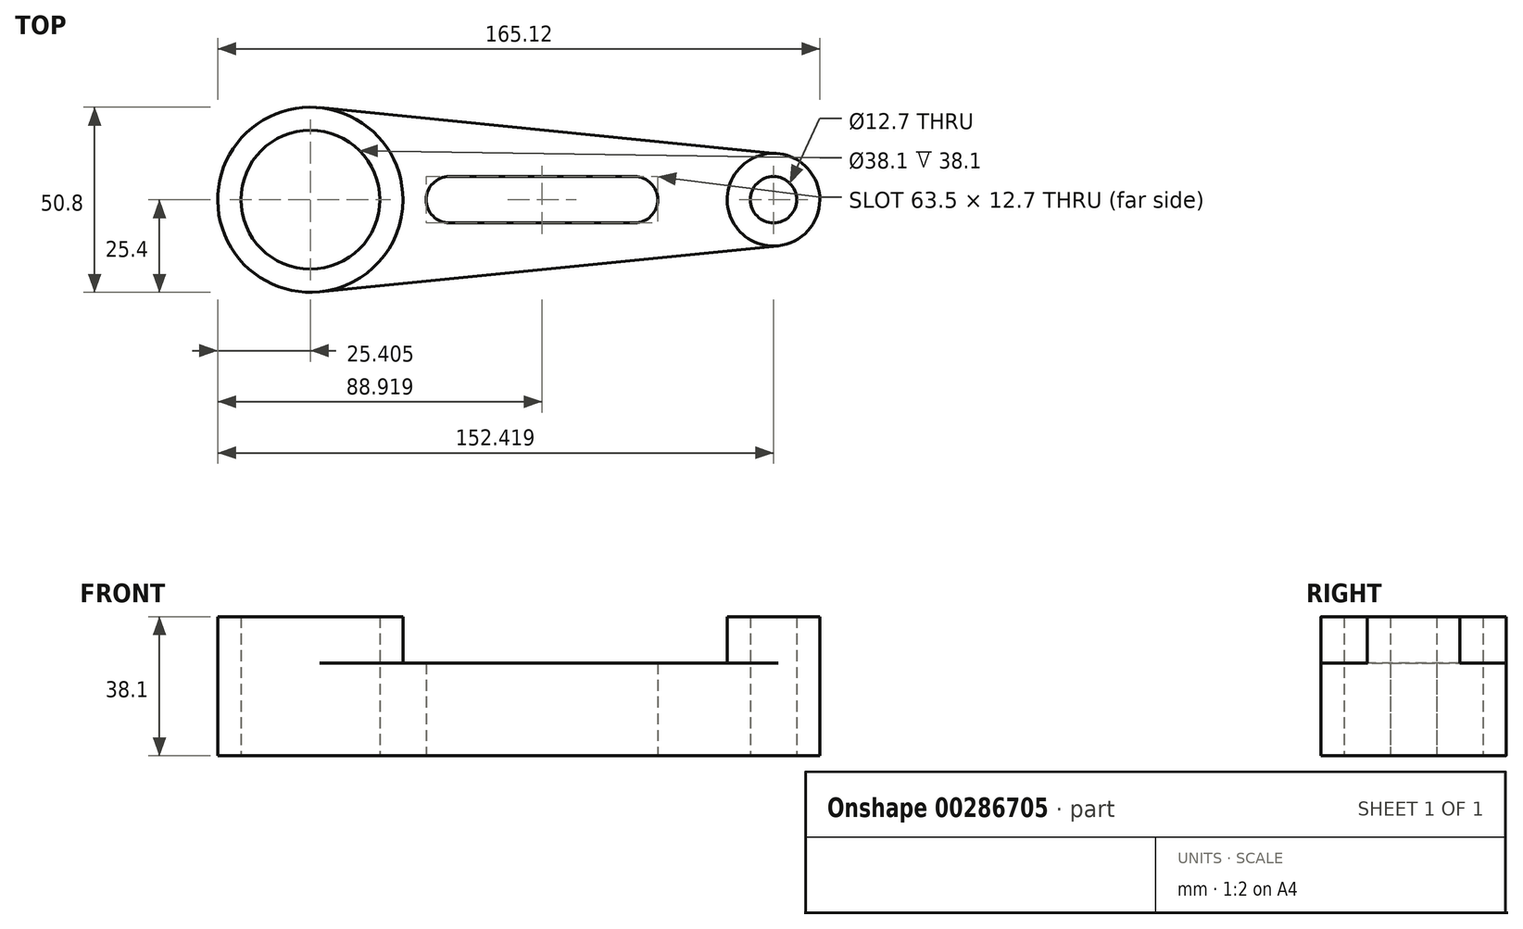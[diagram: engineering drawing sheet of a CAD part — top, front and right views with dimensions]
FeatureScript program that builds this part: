
annotation { "Feature Type Name" : "Feature", "Feature Type Description" : "" }
export const myFeature = defineFeature(function(context is Context, id is Id, definition is map)
    precondition{}
    {
        {
            var Q0;
            Q0=qCreatedBy(makeId("Top.planeOp"),FACE);
            var sketch = newSketch(context, id + "F0", { "sketchPlane" : qUnion([Q0])});
            skCircle(sketch, "E0", {"center": v(108.8, 0) * mm, "radius": 6.35 * mm});
            skCircle(sketch, "E1", {"center": v(108.8, 0) * mm, "radius": 12.7 * mm});
            skCircle(sketch, "E2", {"center": v(-18.2, 0) * mm, "radius": 19.05 * mm});
            skCircle(sketch, "E3", {"center": v(-18.2, 0) * mm, "radius": 25.4 * mm});
            skLineSegment(sketch, "E4", {"start": v(-15.67, 25.27) * mm, "end": v(110.08, 12.64) * mm});
            skLineSegment(sketch, "E5", {"start": v(-15.67, -25.27) * mm, "end": v(110.08, -12.64) * mm});
            skCircle(sketch, "E6", {"center": v(70.7, 0) * mm, "radius": 6.35 * mm});
            skCircle(sketch, "E7", {"center": v(19.9, 0) * mm, "radius": 6.35 * mm});
            skLineSegment(sketch, "E8", {"start": v(19.9, -6.35) * mm, "end": v(70.7, -6.35) * mm});
            skLineSegment(sketch, "E9", {"start": v(19.9, 6.35) * mm, "end": v(70.7, 6.35) * mm});
            skSolve(sketch);
        }
        {
            var Q0;
            {var subQ1=sQuery(id+"F0.wireOp",EDGE,"E4");Q0=makeQuery(id+"F0.imprint","IMPRINT",FACE,{"disambiguationData":[TD([[makeQuery(id+"F0.imprint","IMPRINT",EDGE,{"derivedFrom":subQ1}),-1.0]])]});}
            extrude(context, id + "F1", {"entities" : qUnion([Q0]), "depth" : 25.4 * mm});
        }
        {
            var Q0;
            Q0=makeQuery(id+"F0.imprint","IMPRINT",FACE,{"disambiguationData":[TD([[makeQuery(id+"F0.imprint","IMPRINT",EDGE,{"derivedFrom":sQuery(id+"F0.wireOp",EDGE,"E2")}),-1.0]])]});
            var Q1;
            Q1=makeQuery(id+"F0.imprint","IMPRINT",FACE,{"disambiguationData":[TD([[makeQuery(id+"F0.imprint","IMPRINT",EDGE,{"derivedFrom":sQuery(id+"F0.wireOp",EDGE,"E0")}),-1.0]])]});
            extrude(context, id + "F2", {"entities" : qUnion([Q0, Q1]), "operationType" : NewBodyOperationType.ADD, "depth" : 38.1 * mm});
        }
    });
